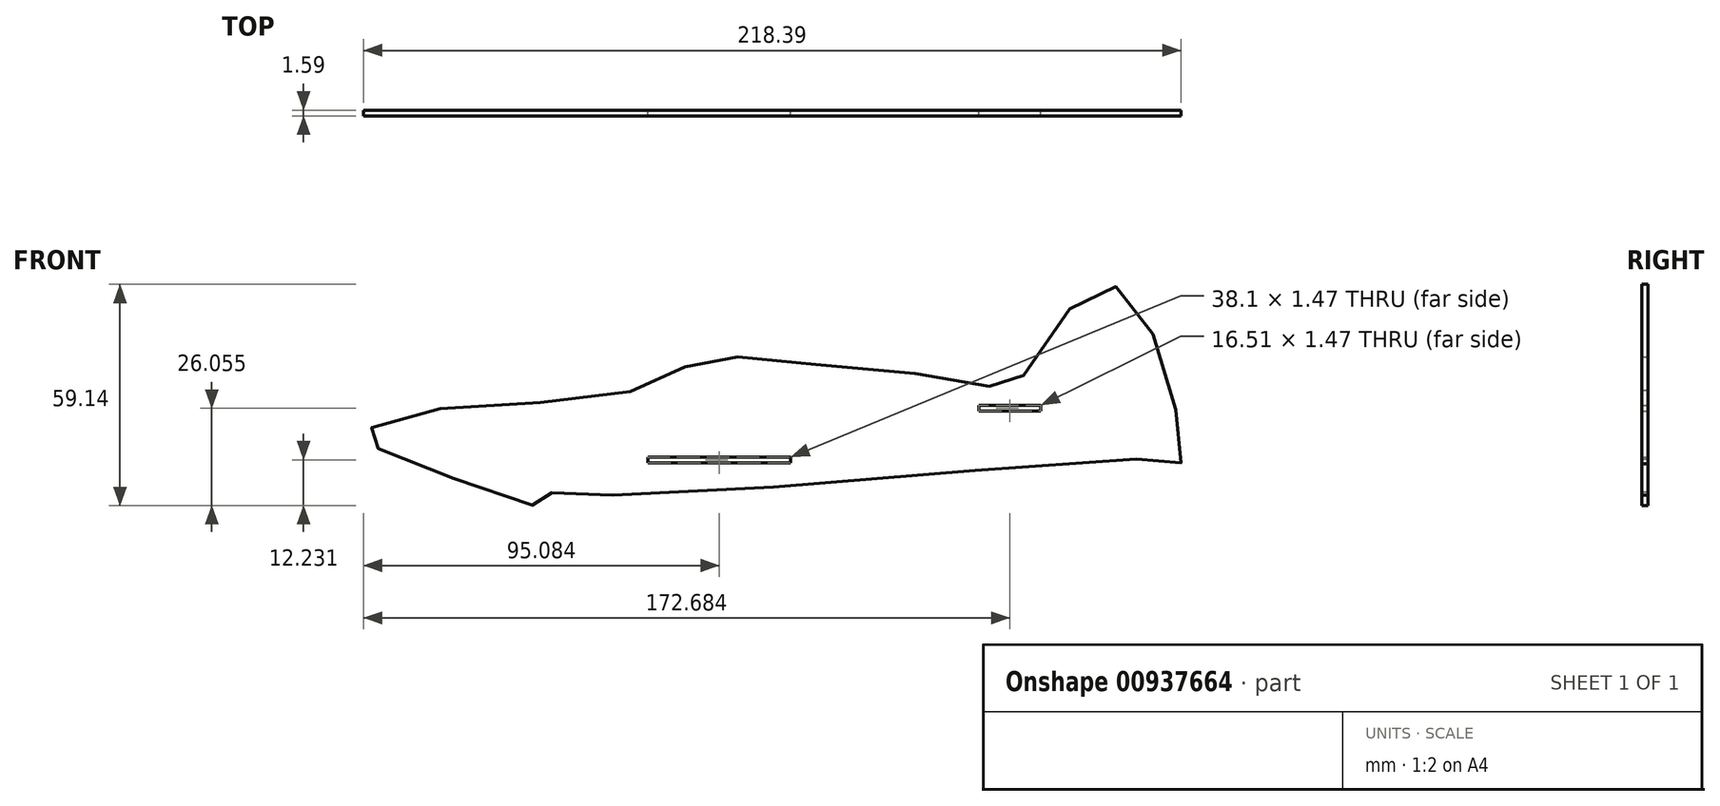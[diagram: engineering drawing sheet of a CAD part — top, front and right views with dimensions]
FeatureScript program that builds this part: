
annotation { "Feature Type Name" : "Feature", "Feature Type Description" : "" }
export const myFeature = defineFeature(function(context is Context, id is Id, definition is map)
    precondition{}
    {
        {
            var Q0;
            Q0=qCreatedBy(makeId("Front.planeOp"),FACE);
            var sketch = newSketch(context, id + "F0", { "sketchPlane" : qUnion([Q0])});
            skLineSegment(sketch, "E0.bottom", {"start": v(-114.3, 50.8) * mm, "end": v(114.3, 50.8) * mm, "construction": true});
            skLineSegment(sketch, "E0.top", {"start": v(-114.3, -50.8) * mm, "end": v(114.3, -50.8) * mm, "construction": true});
            skLineSegment(sketch, "E0.left", {"start": v(-114.3, 50.8) * mm, "end": v(-114.3, -50.8) * mm, "construction": true});
            skLineSegment(sketch, "E0.right", {"start": v(114.3, 50.8) * mm, "end": v(114.3, -50.8) * mm, "construction": true});
            skPoint(sketch, "E0.middle", {"position": v(0, 0) * mm});
            skFitSpline(sketch, "E1", {"points": [v(-38.18, 11.96) * mm, v(-92.78, 6.82) * mm, v(-109.48, 0) * mm, v(-96.63, -6.67) * mm, v(-61.3, -18.23) * mm, v(-60.02, -15.66) * mm, v(-42.68, -15.66) * mm, v(108.26, -6.67) * mm, v(108.9, -7.31) * mm, v(107.62, 6.18) * mm, v(95.41, 37) * mm, v(83.85, 38.93) * mm, v(63.94, 13.24) * mm, v(56.23, 13.88) * mm, v(7.42, 19.67) * mm, v(-19.56, 20.3) * mm, v(-38.18, 11.96) * mm]});
            skLineSegment(sketch, "E2.bottom", {"start": v(71.46, 8.3) * mm, "end": v(54.95, 8.3) * mm});
            skLineSegment(sketch, "E2.top", {"start": v(71.46, 6.83) * mm, "end": v(54.95, 6.83) * mm});
            skLineSegment(sketch, "E2.left", {"start": v(71.46, 8.3) * mm, "end": v(71.46, 6.83) * mm});
            skLineSegment(sketch, "E2.right", {"start": v(54.95, 8.3) * mm, "end": v(54.95, 6.83) * mm});
            skPoint(sketch, "E2.middle", {"position": v(63.2, 7.56) * mm});
            skLineSegment(sketch, "E3.left", {"start": v(0, -13.54) * mm, "end": v(0, -12.07) * mm});
            skLineSegment(sketch, "E3.right", {"start": v(-38.1, -13.54) * mm, "end": v(-38.1, -12.07) * mm});
            skPoint(sketch, "E3.middle", {"position": v(-19.05, -12.8) * mm});
            skLineSegment(sketch, "E4.bottom", {"start": v(-33.45, -5.52) * mm, "end": v(4.65, -5.52) * mm});
            skLineSegment(sketch, "E4.top", {"start": v(-33.45, -7) * mm, "end": v(4.65, -7) * mm});
            skLineSegment(sketch, "E4.left", {"start": v(-33.45, -5.52) * mm, "end": v(-33.45, -7) * mm});
            skLineSegment(sketch, "E4.right", {"start": v(4.65, -5.52) * mm, "end": v(4.65, -7) * mm});
            skPoint(sketch, "E4.middle", {"position": v(-14.4, -6.26) * mm});
            skSolve(sketch);
        }
        {
            var Q0;
            Q0 = qSketchRegion(id + "F0", true);
            extrude(context, id + "F1", {"entities" : qUnion([Q0]), "depth" : 1.59 * mm, "offsetDistance" : 25.4 * mm});
        }
    });
